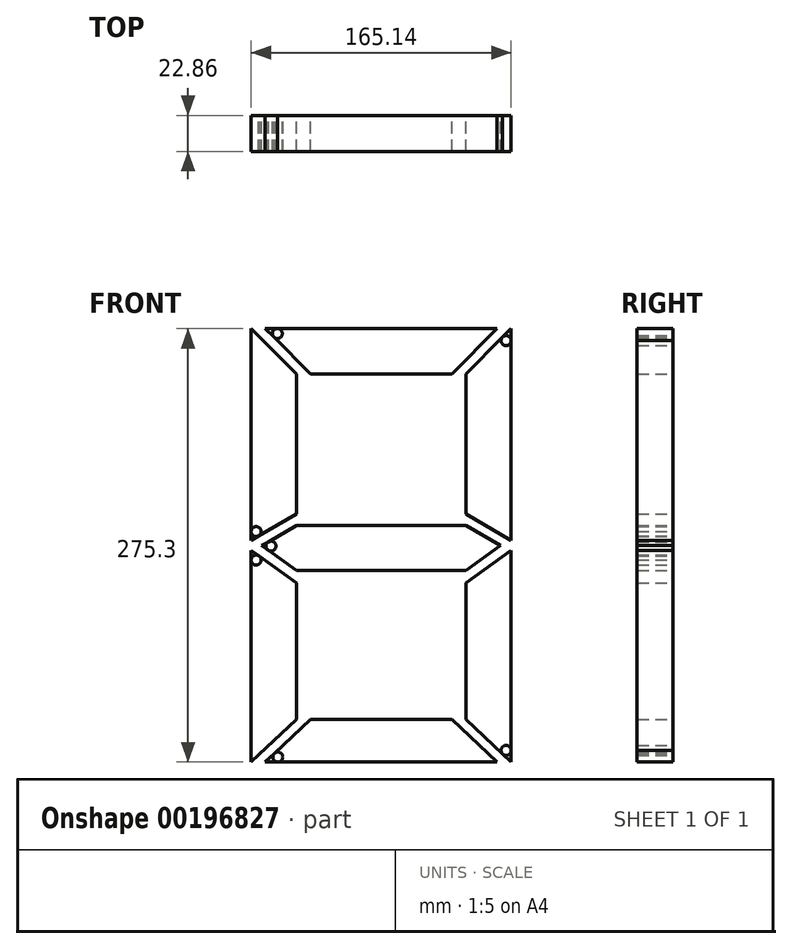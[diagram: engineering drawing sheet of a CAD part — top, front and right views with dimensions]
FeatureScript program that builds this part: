
annotation { "Feature Type Name" : "Feature", "Feature Type Description" : "" }
export const myFeature = defineFeature(function(context is Context, id is Id, definition is map)
    precondition{}
    {
        {
            var Q0;
            Q0=qCreatedBy(makeId("Front.planeOp"),FACE);
            var sketch = newSketch(context, id + "F0", { "sketchPlane" : qUnion([Q0])});
            skLineSegment(sketch, "E0.left", {"start": v(13.55, -44.45) * mm, "end": v(13.55, 44.45) * mm});
            skLineSegment(sketch, "E1", {"start": v(22.53, 44.45) * mm, "end": v(112.25, 44.45) * mm});
            skLineSegment(sketch, "E2", {"start": v(121.23, -44.45) * mm, "end": v(121.23, 44.45) * mm});
            skLineSegment(sketch, "E3.bottom", {"start": v(-27.88, 85.89) * mm, "end": v(161.85, 85.89) * mm});
            skLineSegment(sketch, "E3.top", {"start": v(-27.88, -214.8) * mm, "end": v(161.85, -214.8) * mm});
            skLineSegment(sketch, "E3.left", {"start": v(-27.88, 85.89) * mm, "end": v(-27.88, -214.8) * mm});
            skLineSegment(sketch, "E3.right", {"start": v(161.85, 85.89) * mm, "end": v(161.85, -214.8) * mm});
            skLineSegment(sketch, "E4", {"start": v(149.97, 73.19) * mm, "end": v(121.23, 44.45) * mm});
            skLineSegment(sketch, "E5", {"start": v(112.25, 44.45) * mm, "end": v(140.99, 73.19) * mm});
            skLineSegment(sketch, "E6", {"start": v(121.23, -174.9) * mm, "end": v(149.97, -202.1) * mm});
            skLineSegment(sketch, "E7", {"start": v(121.23, -88.37) * mm, "end": v(121.23, -174.9) * mm});
            skLineSegment(sketch, "E8", {"start": v(121.23, -88.37) * mm, "end": v(149.97, -67.64) * mm});
            skLineSegment(sketch, "E9", {"start": v(149.97, -61.3) * mm, "end": v(121.23, -44.45) * mm});
            skLineSegment(sketch, "E10", {"start": v(149.97, 73.19) * mm, "end": v(149.97, -61.3) * mm});
            skLineSegment(sketch, "E11", {"start": v(149.97, -202.1) * mm, "end": v(149.97, -67.64) * mm});
            skLineSegment(sketch, "E12", {"start": v(121.23, -51.81) * mm, "end": v(143.2, -64.69) * mm});
            skLineSegment(sketch, "E13", {"start": v(121.23, -80.54) * mm, "end": v(143.2, -64.69) * mm});
            skLineSegment(sketch, "E14", {"start": v(-15.17, -61.3) * mm, "end": v(-15.17, 73.19) * mm});
            skLineSegment(sketch, "E15", {"start": v(-15.17, -61.3) * mm, "end": v(13.55, -44.45) * mm});
            skLineSegment(sketch, "E16", {"start": v(121.23, -51.81) * mm, "end": v(13.55, -51.81) * mm});
            skLineSegment(sketch, "E17", {"start": v(13.55, -51.81) * mm, "end": v(-8.41, -64.69) * mm});
            skLineSegment(sketch, "E18", {"start": v(121.23, -80.54) * mm, "end": v(13.55, -80.54) * mm});
            skLineSegment(sketch, "E19", {"start": v(-8.41, -64.69) * mm, "end": v(13.55, -80.54) * mm});
            skLineSegment(sketch, "E20", {"start": v(-15.17, -67.64) * mm, "end": v(-15.17, -202.1) * mm});
            skLineSegment(sketch, "E21", {"start": v(-15.17, -67.64) * mm, "end": v(13.55, -88.37) * mm});
            skLineSegment(sketch, "E22", {"start": v(13.55, -88.37) * mm, "end": v(13.55, -174.9) * mm});
            skLineSegment(sketch, "E23", {"start": v(13.55, -174.9) * mm, "end": v(-15.17, -202.1) * mm});
            skLineSegment(sketch, "E24", {"start": v(140.99, 73.19) * mm, "end": v(-6.2, 73.19) * mm});
            skLineSegment(sketch, "E25", {"start": v(13.55, 44.45) * mm, "end": v(-15.17, 73.19) * mm});
            skLineSegment(sketch, "E26", {"start": v(22.53, 44.45) * mm, "end": v(-6.2, 73.19) * mm});
            skLineSegment(sketch, "E27", {"start": v(22.53, -174.9) * mm, "end": v(112.25, -174.9) * mm});
            skLineSegment(sketch, "E28", {"start": v(22.53, -174.9) * mm, "end": v(-6.2, -202.1) * mm});
            skLineSegment(sketch, "E29", {"start": v(-6.2, -202.1) * mm, "end": v(140.99, -202.1) * mm});
            skLineSegment(sketch, "E30", {"start": v(112.25, -174.9) * mm, "end": v(140.99, -202.1) * mm});
            skLineSegment(sketch, "E31", {"start": v(-15.17, 73.19) * mm, "end": v(-6.2, 73.19) * mm});
            skLineSegment(sketch, "E32", {"start": v(140.99, 73.19) * mm, "end": v(149.97, 73.19) * mm});
            skLineSegment(sketch, "E33", {"start": v(149.97, -202.1) * mm, "end": v(140.99, -202.1) * mm});
            skLineSegment(sketch, "E34", {"start": v(-6.2, -202.1) * mm, "end": v(-15.17, -202.1) * mm});
            skLineSegment(sketch, "E35", {"start": v(-15.17, -67.64) * mm, "end": v(-15.17, -61.3) * mm});
            skLineSegment(sketch, "E36", {"start": v(-8.41, -64.69) * mm, "end": v(-15.39, -64.69) * mm});
            skLineSegment(sketch, "E37", {"start": v(149.97, -61.3) * mm, "end": v(149.97, -67.64) * mm});
            skLineSegment(sketch, "E38", {"start": v(143.2, -64.69) * mm, "end": v(149.97, -64.69) * mm});
            skPoint(sketch, "E38.endSnap0", {"position": v(149.97, -64.47) * mm});
            skLineSegment(sketch, "E39", {"start": v(13.55, -51.81) * mm, "end": v(13.55, -51.81) * mm});
            skSolve(sketch);
        }
        {
            var Q0;
            Q0=makeQuery(id+"F0.imprint","IMPRINT",FACE,{"disambiguationData":[TD([[makeQuery(id+"F0.imprint","IMPRINT",EDGE,{"derivedFrom":sQuery(id+"F0.wireOp",EDGE,"E0.left")}),1.0]])]});
            var Q1;
            Q1=makeQuery(id+"F0.imprint","IMPRINT",FACE,{"disambiguationData":[TD([[makeQuery(id+"F0.imprint","IMPRINT",EDGE,{"derivedFrom":sQuery(id+"F0.wireOp",EDGE,"E1")}),1.0]])]});
            var Q2;
            Q2=makeQuery(id+"F0.imprint","IMPRINT",FACE,{"disambiguationData":[TD([[makeQuery(id+"F0.imprint","IMPRINT",EDGE,{"derivedFrom":sQuery(id+"F0.wireOp",EDGE,"E6")}),1.0]])]});
            var Q3;
            Q3=makeQuery(id+"F0.imprint","IMPRINT",FACE,{"disambiguationData":[TD([[makeQuery(id+"F0.imprint","IMPRINT",EDGE,{"derivedFrom":sQuery(id+"F0.wireOp",EDGE,"E12")}),-1.0]])]});
            var Q4;
            Q4=makeQuery(id+"F0.imprint","IMPRINT",FACE,{"disambiguationData":[TD([[makeQuery(id+"F0.imprint","IMPRINT",EDGE,{"derivedFrom":sQuery(id+"F0.wireOp",EDGE,"E20")}),1.0]])]});
            var Q5;
            Q5=makeQuery(id+"F0.imprint","IMPRINT",FACE,{"disambiguationData":[TD([[makeQuery(id+"F0.imprint","IMPRINT",EDGE,{"derivedFrom":sQuery(id+"F0.wireOp",EDGE,"E27")}),-1.0]])]});
            var Q6;
            Q6=makeQuery(id+"F0.imprint","IMPRINT",FACE,{"disambiguationData":[TD([[makeQuery(id+"F0.imprint","IMPRINT",EDGE,{"derivedFrom":sQuery(id+"F0.wireOp",EDGE,"E2")}),-1.0]])]});
            extrude(context, id + "F1", {"entities" : qUnion([Q0, Q1, Q2, Q3, Q4, Q5, Q6]), "depth" : 22.86 * mm, "offsetDistance" : 25.4 * mm});
        }
        {
            var Q0;
            Q0=makeQuery(id+"F0.imprint","IMPRINT",FACE,{"disambiguationData":[TD([[makeQuery(id+"F0.imprint","IMPRINT",EDGE,{"derivedFrom":sQuery(id+"F0.wireOp",EDGE,"E12")}),-1.0]])]});
            var sketch = newSketch(context, id + "F2", { "sketchPlane" : qUnion([Q0])});
            skCircle(sketch, "E40", {"center": v(-12, -55.75) * mm, "radius": 3.18 * mm});
            skCircle(sketch, "E41", {"center": v(-12, -73.85) * mm, "radius": 3.18 * mm});
            skCircle(sketch, "E42", {"center": v(-2.6, -64.96) * mm, "radius": 3.18 * mm});
            skCircle(sketch, "E43", {"center": v(1.77, -198.93) * mm, "radius": 3.18 * mm});
            skCircle(sketch, "E44", {"center": v(146.8, -194.73) * mm, "radius": 3.18 * mm});
            skCircle(sketch, "E45", {"center": v(1.47, 70.01) * mm, "radius": 3.18 * mm});
            skCircle(sketch, "E46", {"center": v(146.8, 65.52) * mm, "radius": 3.18 * mm});
            skSolve(sketch);
        }
        {
            var Q0;
            Q0 = qSketchRegion(id + "F2", true);
            var Q1;
            Q1=sQuery(id+"F2.wireOp",EDGE,"E46");
            var Q2;
            Q2=sQuery(id+"F2.wireOp",EDGE,"E45");
            var Q3;
            Q3=sQuery(id+"F2.wireOp",EDGE,"E40");
            extrude(context, id + "F3", {"entities" : qUnion([Q0]), "operationType" : NewBodyOperationType.REMOVE, "surfaceEntities" : qUnion([Q1, Q2, Q3]), "depth" : 25.4 * mm, "offsetDistance" : 25.4 * mm});
        }
    });
